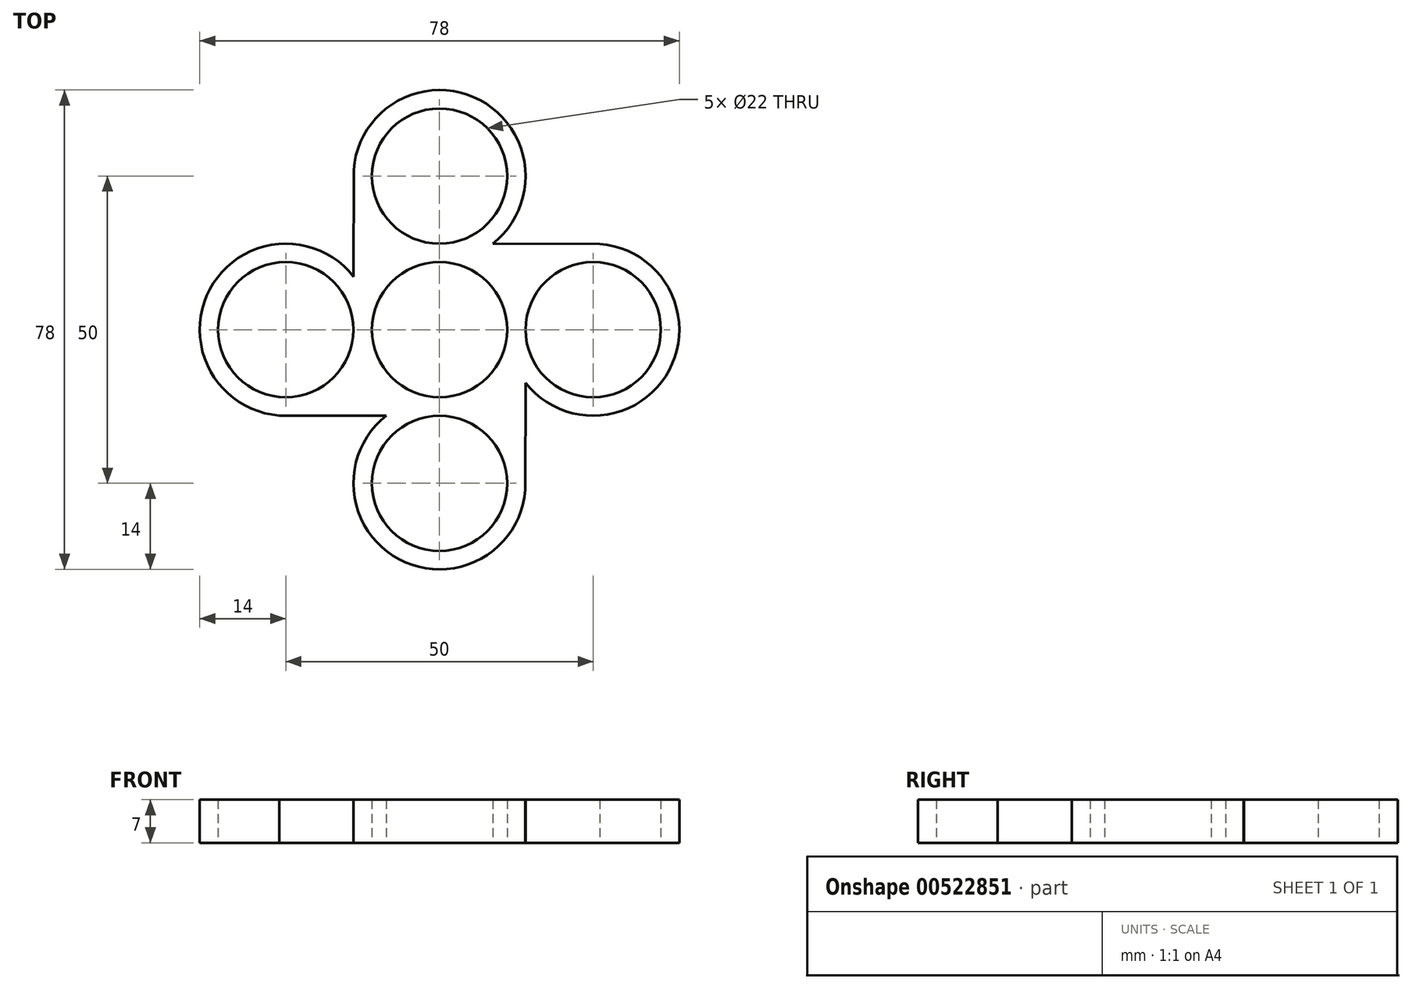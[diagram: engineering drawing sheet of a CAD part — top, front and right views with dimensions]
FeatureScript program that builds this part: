
annotation { "Feature Type Name" : "Feature", "Feature Type Description" : "" }
export const myFeature = defineFeature(function(context is Context, id is Id, definition is map)
    precondition{}
    {
        {
            var Q0;
            Q0=qCreatedBy(makeId("Top.planeOp"),FACE);
            var sketch = newSketch(context, id + "F0", { "sketchPlane" : qUnion([Q0])});
            skCircle(sketch, "E0", {"center": v(0, 0) * mm, "radius": 11 * mm});
            skCircle(sketch, "E1", {"center": v(0, 0) * mm, "radius": 14 * mm});
            skCircle(sketch, "E2", {"center": v(0, 25) * mm, "radius": 11 * mm});
            skCircle(sketch, "E3", {"center": v(0, 25) * mm, "radius": 14 * mm});
            skCircle(sketch, "E4.1.0", {"center": v(-25, 0) * mm, "radius": 11 * mm});
            skCircle(sketch, "E4.1.1", {"center": v(-25, 0) * mm, "radius": 14 * mm});
            skCircle(sketch, "E4.2.0", {"center": v(0, -25) * mm, "radius": 11 * mm});
            skCircle(sketch, "E4.2.1", {"center": v(0, -25) * mm, "radius": 14 * mm});
            skCircle(sketch, "E4.3.0", {"center": v(25, 0) * mm, "radius": 11 * mm});
            skCircle(sketch, "E4.3.1", {"center": v(25, 0) * mm, "radius": 14 * mm});
            skLineSegment(sketch, "E5", {"start": v(-14, 0) * mm, "end": v(-13.96, 26.04) * mm});
            skLineSegment(sketch, "E6.1.0", {"start": v(0, -14) * mm, "end": v(-26.04, -13.96) * mm});
            skLineSegment(sketch, "E6.2.0", {"start": v(14, 0) * mm, "end": v(13.96, -26.04) * mm});
            skLineSegment(sketch, "E6.3.0", {"start": v(0, 14) * mm, "end": v(26.04, 13.96) * mm});
            skPoint(sketch, "E7.endSnap0", {"position": v(13.02, 13.98) * mm});
            skSolve(sketch);
        }
        {
            var Q0;
            {var subQ5=sQuery(id+"F0.wireOp",EDGE,"E4.1.0");Q0=makeQuery(id+"F0.imprint","IMPRINT",FACE,{"disambiguationData":[TD([[makeQuery(id+"F0.imprint","IMPRINT",EDGE,{"derivedFrom":subQ5}),-1.0]])]});}
            var Q1;
            {var subQ0=sQuery(id+"F0.wireOp",EDGE,"E4.1.1");var subQ1=sQuery(id+"F0.wireOp",EDGE,"E1");var subQ2=makeQuery(id+"F0.imprint","INTERSECT",VERTEX,{"disambiguationData":[OD(1.0)],"derivedFrom":[subQ1,subQ0]});Q1=makeQuery(id+"F0.imprint","IMPRINT",FACE,{"disambiguationData":[TD([[makeQuery(id+"F0.imprint","IMPRINT",EDGE,{"disambiguationData":[TD([[subQ2,-1.0]])],"derivedFrom":subQ1}),-1.0]])]});}
            var Q2;
            {var subQ0=sQuery(id+"F0.wireOp",EDGE,"E4.2.0");Q2=makeQuery(id+"F0.imprint","IMPRINT",FACE,{"disambiguationData":[TD([[makeQuery(id+"F0.imprint","IMPRINT",EDGE,{"derivedFrom":subQ0}),-1.0]])]});}
            var Q3;
            {var subQ2=sQuery(id+"F0.wireOp",EDGE,"E1");var subQ4=makeQuery(id+"F0.imprint","INTERSECT",VERTEX,{"derivedFrom":[subQ2,sQuery(id+"F0.wireOp",EDGE,"E6.1.0")]});Q3=makeQuery(id+"F0.imprint","IMPRINT",FACE,{"disambiguationData":[TD([[makeQuery(id+"F0.imprint","IMPRINT",EDGE,{"disambiguationData":[TD([[subQ4,1.0]])],"derivedFrom":subQ2}),1.0]])]});}
            var Q4;
            {var subQ0=sQuery(id+"F0.wireOp",EDGE,"E6.1.0");var subQ1=sQuery(id+"F0.wireOp",EDGE,"E1");var subQ2=makeQuery(id+"F0.imprint","INTERSECT",VERTEX,{"derivedFrom":[subQ1,subQ0]});Q4=makeQuery(id+"F0.imprint","IMPRINT",FACE,{"disambiguationData":[TD([[makeQuery(id+"F0.imprint","IMPRINT",EDGE,{"disambiguationData":[TD([[subQ2,1.0]])],"derivedFrom":subQ1}),-1.0]])]});}
            var Q5;
            {var subQ0=sQuery(id+"F0.wireOp",EDGE,"E4.1.1");var subQ1=sQuery(id+"F0.wireOp",EDGE,"E0");var subQ2=makeQuery(id+"F0.imprint","INTERSECT",VERTEX,{"derivedFrom":[subQ1,subQ0]});Q5=makeQuery(id+"F0.imprint","IMPRINT",FACE,{"disambiguationData":[TD([[makeQuery(id+"F0.imprint","IMPRINT",EDGE,{"disambiguationData":[TD([[subQ2,-1.0]])],"derivedFrom":subQ1}),-1.0]])]});}
            var Q6;
            {var subQ0=sQuery(id+"F0.wireOp",EDGE,"E1");var subQ4=makeQuery(id+"F0.imprint","INTERSECT",VERTEX,{"derivedFrom":[subQ0,sQuery(id+"F0.wireOp",EDGE,"E5")]});Q6=makeQuery(id+"F0.imprint","IMPRINT",FACE,{"disambiguationData":[TD([[makeQuery(id+"F0.imprint","IMPRINT",EDGE,{"disambiguationData":[TD([[subQ4,1.0]])],"derivedFrom":subQ0}),1.0]])]});}
            var Q7;
            {var subQ0=sQuery(id+"F0.wireOp",EDGE,"E5");var subQ1=sQuery(id+"F0.wireOp",EDGE,"E1");var subQ2=makeQuery(id+"F0.imprint","INTERSECT",VERTEX,{"derivedFrom":[subQ1,subQ0]});Q7=makeQuery(id+"F0.imprint","IMPRINT",FACE,{"disambiguationData":[TD([[makeQuery(id+"F0.imprint","IMPRINT",EDGE,{"disambiguationData":[TD([[subQ2,1.0]])],"derivedFrom":subQ1}),-1.0]])]});}
            var Q8;
            {var subQ0=sQuery(id+"F0.wireOp",EDGE,"E3");var subQ1=sQuery(id+"F0.wireOp",EDGE,"E0");var subQ2=makeQuery(id+"F0.imprint","INTERSECT",VERTEX,{"derivedFrom":[subQ1,subQ0]});Q8=makeQuery(id+"F0.imprint","IMPRINT",FACE,{"disambiguationData":[TD([[makeQuery(id+"F0.imprint","IMPRINT",EDGE,{"disambiguationData":[TD([[subQ2,-1.0]])],"derivedFrom":subQ1}),-1.0]])]});}
            var Q9;
            {var subQ0=sQuery(id+"F0.wireOp",EDGE,"E3");var subQ1=sQuery(id+"F0.wireOp",EDGE,"E1");var subQ2=makeQuery(id+"F0.imprint","INTERSECT",VERTEX,{"disambiguationData":[OD(1.0)],"derivedFrom":[subQ1,subQ0]});Q9=makeQuery(id+"F0.imprint","IMPRINT",FACE,{"disambiguationData":[TD([[makeQuery(id+"F0.imprint","IMPRINT",EDGE,{"disambiguationData":[TD([[subQ2,-1.0]])],"derivedFrom":subQ1}),-1.0]])]});}
            var Q10;
            {var subQ0=sQuery(id+"F0.wireOp",EDGE,"E2");Q10=makeQuery(id+"F0.imprint","IMPRINT",FACE,{"disambiguationData":[TD([[makeQuery(id+"F0.imprint","IMPRINT",EDGE,{"derivedFrom":subQ0}),-1.0]])]});}
            var Q11;
            {var subQ2=sQuery(id+"F0.wireOp",EDGE,"E1");var subQ5=makeQuery(id+"F0.imprint","INTERSECT",VERTEX,{"derivedFrom":[subQ2,sQuery(id+"F0.wireOp",EDGE,"E6.3.0")]});Q11=makeQuery(id+"F0.imprint","IMPRINT",FACE,{"disambiguationData":[TD([[makeQuery(id+"F0.imprint","IMPRINT",EDGE,{"disambiguationData":[TD([[subQ5,1.0]])],"derivedFrom":subQ2}),1.0]])]});}
            var Q12;
            {var subQ0=sQuery(id+"F0.wireOp",EDGE,"E6.3.0");var subQ1=sQuery(id+"F0.wireOp",EDGE,"E1");var subQ2=makeQuery(id+"F0.imprint","INTERSECT",VERTEX,{"derivedFrom":[subQ1,subQ0]});Q12=makeQuery(id+"F0.imprint","IMPRINT",FACE,{"disambiguationData":[TD([[makeQuery(id+"F0.imprint","IMPRINT",EDGE,{"disambiguationData":[TD([[subQ2,1.0]])],"derivedFrom":subQ1}),-1.0]])]});}
            var Q13;
            {var subQ0=sQuery(id+"F0.wireOp",EDGE,"E3");var subQ1=sQuery(id+"F0.wireOp",EDGE,"E0");var subQ2=makeQuery(id+"F0.imprint","INTERSECT",VERTEX,{"derivedFrom":[subQ1,subQ0]});Q13=makeQuery(id+"F0.imprint","IMPRINT",FACE,{"disambiguationData":[TD([[makeQuery(id+"F0.imprint","IMPRINT",EDGE,{"disambiguationData":[TD([[subQ2,1.0]])],"derivedFrom":subQ1}),-1.0]])]});}
            var Q14;
            {var subQ0=sQuery(id+"F0.wireOp",EDGE,"E4.3.1");var subQ1=sQuery(id+"F0.wireOp",EDGE,"E1");var subQ2=makeQuery(id+"F0.imprint","INTERSECT",VERTEX,{"disambiguationData":[OD(0.0)],"derivedFrom":[subQ1,subQ0]});Q14=makeQuery(id+"F0.imprint","IMPRINT",FACE,{"disambiguationData":[TD([[makeQuery(id+"F0.imprint","IMPRINT",EDGE,{"disambiguationData":[TD([[subQ2,-1.0]])],"derivedFrom":subQ1}),-1.0]])]});}
            var Q15;
            {var subQ0=sQuery(id+"F0.wireOp",EDGE,"E1");var subQ6=makeQuery(id+"F0.imprint","INTERSECT",VERTEX,{"derivedFrom":[subQ0,sQuery(id+"F0.wireOp",EDGE,"E4.3.0")]});Q15=makeQuery(id+"F0.imprint","IMPRINT",FACE,{"disambiguationData":[TD([[makeQuery(id+"F0.imprint","IMPRINT",EDGE,{"disambiguationData":[TD([[subQ6,-1.0]])],"derivedFrom":subQ0}),1.0]])]});}
            var Q16;
            {var subQ0=sQuery(id+"F0.wireOp",EDGE,"E6.2.0");var subQ1=sQuery(id+"F0.wireOp",EDGE,"E1");var subQ2=makeQuery(id+"F0.imprint","INTERSECT",VERTEX,{"derivedFrom":[subQ1,subQ0]});Q16=makeQuery(id+"F0.imprint","IMPRINT",FACE,{"disambiguationData":[TD([[makeQuery(id+"F0.imprint","IMPRINT",EDGE,{"disambiguationData":[TD([[subQ2,1.0]])],"derivedFrom":subQ1}),-1.0]])]});}
            var Q17;
            {var subQ0=sQuery(id+"F0.wireOp",EDGE,"E4.3.1");var subQ1=sQuery(id+"F0.wireOp",EDGE,"E0");var subQ2=makeQuery(id+"F0.imprint","INTERSECT",VERTEX,{"derivedFrom":[subQ1,subQ0]});Q17=makeQuery(id+"F0.imprint","IMPRINT",FACE,{"disambiguationData":[TD([[makeQuery(id+"F0.imprint","IMPRINT",EDGE,{"disambiguationData":[TD([[subQ2,1.0]])],"derivedFrom":subQ1}),-1.0]])]});}
            var Q18;
            {var subQ0=sQuery(id+"F0.wireOp",EDGE,"E4.2.1");var subQ1=sQuery(id+"F0.wireOp",EDGE,"E1");var subQ2=makeQuery(id+"F0.imprint","INTERSECT",VERTEX,{"disambiguationData":[OD(1.0)],"derivedFrom":[subQ1,subQ0]});Q18=makeQuery(id+"F0.imprint","IMPRINT",FACE,{"disambiguationData":[TD([[makeQuery(id+"F0.imprint","IMPRINT",EDGE,{"disambiguationData":[TD([[subQ2,-1.0]])],"derivedFrom":subQ1}),-1.0]])]});}
            var Q19;
            {var subQ8=sQuery(id+"F0.wireOp",EDGE,"E4.3.0");Q19=makeQuery(id+"F0.imprint","IMPRINT",FACE,{"disambiguationData":[TD([[makeQuery(id+"F0.imprint","IMPRINT",EDGE,{"derivedFrom":subQ8}),-1.0]])]});}
            extrude(context, id + "F1", {"entities" : qUnion([Q0, Q1, Q2, Q3, Q4, Q5, Q6, Q7, Q8, Q9, Q10, Q11, Q12, Q13, Q14, Q15, Q16, Q17, Q18, Q19]), "depth" : 7 * mm, "offsetDistance" : 25 * mm});
        }
    });
